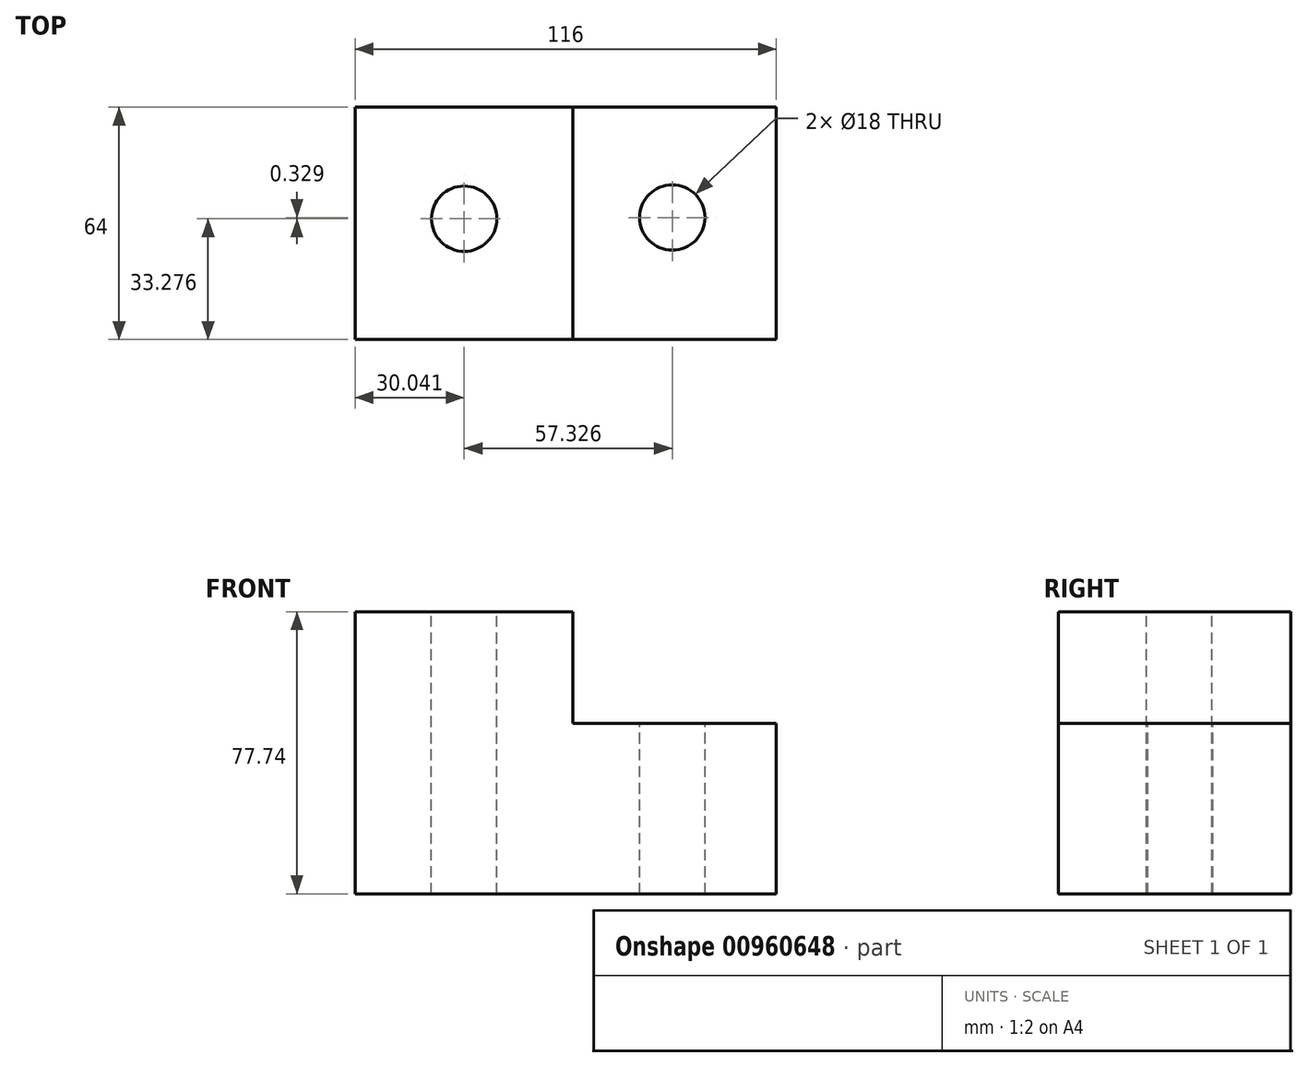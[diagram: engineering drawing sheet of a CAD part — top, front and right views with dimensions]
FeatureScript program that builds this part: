
annotation { "Feature Type Name" : "Feature", "Feature Type Description" : "" }
export const myFeature = defineFeature(function(context is Context, id is Id, definition is map)
    precondition{}
    {
        {
            var Q0;
            Q0=qCreatedBy(makeId("Front.planeOp"),FACE);
            var sketch = newSketch(context, id + "F0", { "sketchPlane" : qUnion([Q0])});
            skLineSegment(sketch, "E0", {"start": v(0, 0) * mm, "end": v(116, 0) * mm});
            skLineSegment(sketch, "E1", {"start": v(116, 0) * mm, "end": v(116, 47) * mm});
            skLineSegment(sketch, "E2", {"start": v(116, 47) * mm, "end": v(60, 47) * mm});
            skLineSegment(sketch, "E3", {"start": v(60, 47) * mm, "end": v(60, 77.74) * mm});
            skLineSegment(sketch, "E4", {"start": v(60, 77.74) * mm, "end": v(0, 77.74) * mm});
            skLineSegment(sketch, "E5", {"start": v(0, 77.74) * mm, "end": v(0, 0) * mm});
            skSolve(sketch);
        }
        {
            var Q0;
            Q0 = qSketchRegion(id + "F0", true);
            extrude(context, id + "F1", {"entities" : qUnion([Q0]), "depth" : 64 * mm, "offsetDistance" : 25 * mm});
        }
        {
            var Q0;
            Q0=makeQuery(id+"F1.opExtrude","SWEPT_FACE",FACE,{"disambiguationData":[OSD([sQuery(id+"F0.wireOp",EDGE,"E4")])]});
            var sketch = newSketch(context, id + "F2", { "sketchPlane" : qUnion([Q0])});
            skCircle(sketch, "E6", {"center": v(30.04, -30.72) * mm, "radius": 9 * mm});
            skCircle(sketch, "E7", {"center": v(87.37, -30.4) * mm, "radius": 9 * mm});
            skSolve(sketch);
        }
        {
            var Q0;
            Q0=makeQuery(id+"F2.imprint","IMPRINT",FACE,{"disambiguationData":[TD([[makeQuery(id+"F2.imprint","IMPRINT",EDGE,{"derivedFrom":sQuery(id+"F2.wireOp",EDGE,"E6")}),1.0]])]});
            var Q1;
            Q1=makeQuery(id+"F2.imprint","IMPRINT",FACE,{"disambiguationData":[TD([[makeQuery(id+"F2.imprint","IMPRINT",EDGE,{"derivedFrom":sQuery(id+"F2.wireOp",EDGE,"E7")}),1.0]])]});
            extrude(context, id + "F3", {"entities" : qUnion([Q0, Q1]), "operationType" : NewBodyOperationType.REMOVE, "oppositeDirection" : true, "depth" : 84 * mm, "offsetDistance" : 25 * mm});
        }
    });
